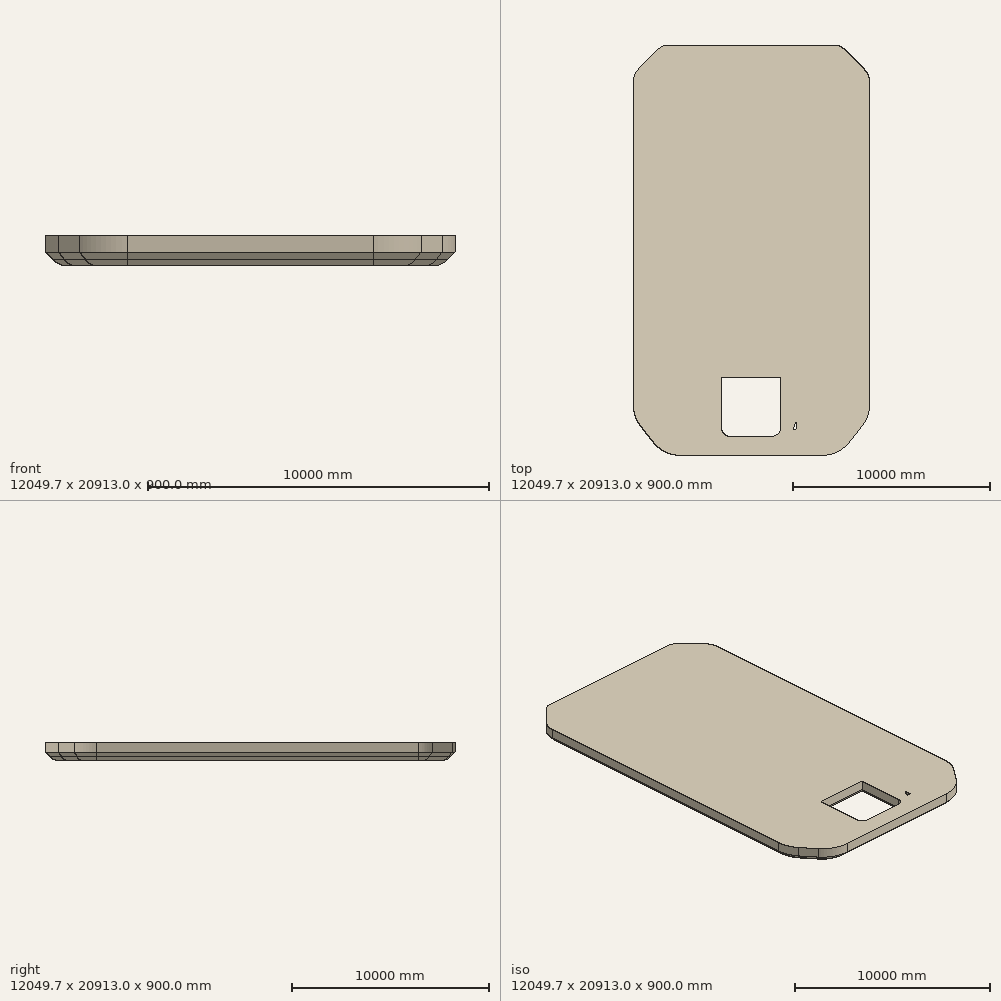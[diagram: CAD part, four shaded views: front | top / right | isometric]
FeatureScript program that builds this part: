
annotation { "Feature Type Name" : "Feature", "Feature Type Description" : "" }
export const myFeature = defineFeature(function(context is Context, id is Id, definition is map)
    precondition{}
    {
        {
            var Q0;
            Q0=qCreatedBy(makeId("Top.planeOp"),FACE);
            var sketch = newSketch(context, id + "F0", { "sketchPlane" : qUnion([Q0])});
            skLineSegment(sketch, "E0.bottom", {"start": v(-3604.76, -10456.52) * mm, "end": v(3572.95, -10456.52) * mm});
            skLineSegment(sketch, "E0.top", {"start": v(-4294.95, 10456.52) * mm, "end": v(4334.31, 10456.52) * mm});
            skLineSegment(sketch, "E0.left", {"start": v(-6024.84, -7867.65) * mm, "end": v(-6024.84, 8560.94) * mm});
            skPoint(sketch, "E0.middle", {"position": v(0, 0) * mm});
            skPoint(sketch, "E1.visualSharp", {"position": v(-6024.84, -10456.52) * mm});
            skLineSegment(sketch, "E2", {"start": v(0, 0) * mm, "end": v(0, -15471.61) * mm, "construction": true});
            skLineSegment(sketch, "E3.0", {"start": v(-4500, 12642.06) * mm, "end": v(-4500, -15471.61) * mm, "construction": true});
            skLineSegment(sketch, "E4.MirrorCS", {"start": v(4500, 12642.06) * mm, "end": v(4500, -15471.61) * mm, "construction": true});
            skLineSegment(sketch, "E5", {"start": v(-5019.92, -9768.88) * mm, "end": v(-5640, -8980) * mm});
            skPoint(sketch, "E6.newPointA", {"position": v(-5200, -10456.52) * mm});
            skPoint(sketch, "E6.newPointB", {"position": v(-4479.4, -10456.52) * mm});
            skArc(sketch, "E6.filletArc", {"start": v(-5019.92, -9768.88) * mm, "mid": v(-4391.45, -10275.51) * mm, "end": v(-3604.76, -10456.52) * mm});
            skArc(sketch, "E7.filletArc", {"start": v(-6024.84, -7867.65) * mm, "mid": v(-5925.91, -8456.17) * mm, "end": v(-5640, -8980) * mm});
            skPoint(sketch, "E8.newPointA", {"position": v(5975.16, -10456.52) * mm});
            skLineSegment(sketch, "E9", {"start": v(6000, 10500) * mm, "end": v(10945.39, 10500) * mm, "construction": true});
            skLineSegment(sketch, "E10.0", {"start": v(6000, 9000) * mm, "end": v(10945.39, 9000) * mm, "construction": true});
            skLineSegment(sketch, "E11.MirrorCS", {"start": v(0, 18000) * mm, "end": v(0, 33471.61) * mm, "construction": true});
            skLineSegment(sketch, "E12.MirrorCS", {"start": v(-4719.21, 10280.79) * mm, "end": v(-5731.95, 9268.05) * mm});
            skPoint(sketch, "E13.newPointA", {"position": v(-6000, 9000) * mm});
            skPoint(sketch, "E13.newPointB", {"position": v(-6024.84, 10543.48) * mm});
            skArc(sketch, "E13.filletArc", {"start": v(-5731.95, 9268.05) * mm, "mid": v(-5948.72, 8943.63) * mm, "end": v(-6024.84, 8560.94) * mm});
            skPoint(sketch, "E14.newPointA", {"position": v(-4500, 10500) * mm});
            skPoint(sketch, "E14.newPointB", {"position": v(-5975.16, 10456.52) * mm});
            skArc(sketch, "E14.filletArc", {"start": v(-4294.95, 10456.52) * mm, "mid": v(-4524.56, 10410.85) * mm, "end": v(-4719.21, 10280.79) * mm});
            skPoint(sketch, "E15.newPointA", {"position": v(6000, 9000) * mm});
            skPoint(sketch, "E16.newPointA", {"position": v(4500, 10500) * mm});
            skPoint(sketch, "E16.newPointB", {"position": v(6024.84, 10456.52) * mm});
            skLineSegment(sketch, "E17.MirrorCS", {"start": v(3604.76, -10456.52) * mm, "end": v(-3572.95, -10456.52) * mm});
            skArc(sketch, "E18.MirrorCS", {"start": v(5019.92, -9768.88) * mm, "mid": v(4391.45, -10275.51) * mm, "end": v(3604.76, -10456.52) * mm});
            skLineSegment(sketch, "E19.MirrorCS", {"start": v(5019.92, -9768.88) * mm, "end": v(5640, -8980) * mm});
            skArc(sketch, "E20.MirrorCS", {"start": v(6024.84, -7867.65) * mm, "mid": v(5925.91, -8456.17) * mm, "end": v(5640, -8980) * mm});
            skLineSegment(sketch, "E21.MirrorCS", {"start": v(6024.84, -7867.65) * mm, "end": v(6024.84, 8560.94) * mm});
            skArc(sketch, "E22.MirrorCS", {"start": v(5731.95, 9268.05) * mm, "mid": v(5948.72, 8943.63) * mm, "end": v(6024.84, 8560.94) * mm});
            skLineSegment(sketch, "E23.MirrorCS", {"start": v(4719.21, 10280.79) * mm, "end": v(5731.95, 9268.05) * mm});
            skArc(sketch, "E24.MirrorCS", {"start": v(4294.95, 10456.52) * mm, "mid": v(4524.56, 10410.85) * mm, "end": v(4719.21, 10280.79) * mm});
            skPoint(sketch, "E25", {"position": v(-1520, -6476.52) * mm});
            skPoint(sketch, "E26", {"position": v(-1520, -9476.52) * mm});
            skPoint(sketch, "E27", {"position": v(1480, -9476.52) * mm});
            skPoint(sketch, "E28", {"position": v(1480, -6476.52) * mm});
            skLineSegment(sketch, "E29", {"start": v(-1520, -6476.52) * mm, "end": v(1480, -6476.52) * mm});
            skLineSegment(sketch, "E30", {"start": v(1080, -9476.52) * mm, "end": v(-1120, -9476.52) * mm});
            skLineSegment(sketch, "E31", {"start": v(-1520, -6476.52) * mm, "end": v(-1520, -9076.52) * mm});
            skLineSegment(sketch, "E32", {"start": v(1480, -6476.52) * mm, "end": v(1480, -9076.52) * mm});
            skArc(sketch, "E33.filletArc", {"start": v(-1520, -9076.52) * mm, "mid": v(-1402.84, -9359.37) * mm, "end": v(-1120, -9476.52) * mm});
            skArc(sketch, "E34.filletArc", {"start": v(1080, -9476.52) * mm, "mid": v(1362.84, -9359.37) * mm, "end": v(1480, -9076.52) * mm});
            skPoint(sketch, "E35", {"position": v(-20, -6476.52) * mm});
            skPoint(sketch, "E36", {"position": v(-20, -9476.52) * mm});
            skLineSegment(sketch, "E37.0", {"start": v(-650, 0) * mm, "end": v(-650, -15471.61) * mm, "construction": true});
            skPoint(sketch, "E38", {"position": v(-650, -9156.52) * mm});
            skPoint(sketch, "E39", {"position": v(-650, -8906.52) * mm});
            skLineSegment(sketch, "E40", {"start": v(-650, -8906.52) * mm, "end": v(-1228.06, -8668.5) * mm});
            skLineSegment(sketch, "E41", {"start": v(2294.01, -8720.57) * mm, "end": v(2514.01, -8720.57) * mm, "construction": true});
            skLineSegment(sketch, "E42", {"start": v(2294.01, -8720.57) * mm, "end": v(2109.42, -9152.8) * mm});
            skLineSegment(sketch, "E43", {"start": v(2109.42, -9152.8) * mm, "end": v(2294.01, -9152.8) * mm});
            skLineSegment(sketch, "E44", {"start": v(2294.01, -8720.57) * mm, "end": v(2294.01, -9445.98) * mm});
            skLineSegment(sketch, "E45.0", {"start": v(1100, -8721.92) * mm, "end": v(1098.33, -8721.92) * mm});
            skLineSegment(sketch, "E46.0", {"start": v(-613.48, -8721.92) * mm, "end": v(-1043.46, -8544.88) * mm});
            skLineSegment(sketch, "E47.0", {"start": v(-699.45, -9156.52) * mm, "end": v(-1478.06, -8835.94) * mm});
            skLineSegment(sketch, "E48", {"start": v(-1043.46, -8544.88) * mm, "end": v(-1043.46, -8044.88) * mm});
            skLineSegment(sketch, "E49.0", {"start": v(-1228.06, -8668.5) * mm, "end": v(-1228.06, -8044.88) * mm});
            skLineSegment(sketch, "E50.0", {"start": v(-1478.06, -8835.94) * mm, "end": v(-1478.06, -8044.88) * mm});
            skLineSegment(sketch, "E51", {"start": v(-1478.06, -8044.88) * mm, "end": v(-1043.46, -8044.88) * mm});
            skLineSegment(sketch, "E52.MirrorCS", {"start": v(699.45, -9156.52) * mm, "end": v(1478.06, -8835.94) * mm});
            skLineSegment(sketch, "E53.MirrorCS", {"start": v(650, -8906.52) * mm, "end": v(1228.06, -8668.5) * mm});
            skLineSegment(sketch, "E54.MirrorCS", {"start": v(613.48, -8721.92) * mm, "end": v(1043.46, -8544.88) * mm});
            skLineSegment(sketch, "E55.MirrorCS", {"start": v(1043.46, -8544.88) * mm, "end": v(1043.46, -8044.88) * mm});
            skLineSegment(sketch, "E56.MirrorCS", {"start": v(1228.06, -8668.5) * mm, "end": v(1228.06, -8044.88) * mm});
            skLineSegment(sketch, "E57.MirrorCS", {"start": v(1478.06, -8835.94) * mm, "end": v(1478.06, -8044.88) * mm});
            skLineSegment(sketch, "E58.MirrorCS", {"start": v(1478.06, -8044.88) * mm, "end": v(1043.46, -8044.88) * mm});
            skLineSegment(sketch, "E59", {"start": v(613.48, -8721.92) * mm, "end": v(699.45, -9156.52) * mm});
            skLineSegment(sketch, "E60", {"start": v(-613.48, -8721.92) * mm, "end": v(-699.45, -9156.52) * mm});
            skLineSegment(sketch, "E61", {"start": v(1043.46, -8544.88) * mm, "end": v(1228.06, -8668.5) * mm});
            skLineSegment(sketch, "E62.0", {"start": v(252, -7876.52) * mm, "end": v(-252, -7876.52) * mm});
            skLineSegment(sketch, "E63.0", {"start": v(1080, -8416.52) * mm, "end": v(1043.46, -8416.52) * mm});
            skLineSegment(sketch, "E64.0", {"start": v(-252, 0) * mm, "end": v(-252, -6476.52) * mm, "construction": true});
            skLineSegment(sketch, "E65.MirrorCS", {"start": v(252, 0) * mm, "end": v(252, -6476.52) * mm, "construction": true});
            skPoint(sketch, "E66", {"position": v(-252, -7876.52) * mm});
            skPoint(sketch, "E67", {"position": v(-252, -8416.52) * mm});
            skPoint(sketch, "E68", {"position": v(252, -8416.52) * mm});
            skPoint(sketch, "E69", {"position": v(252, -7876.52) * mm});
            skLineSegment(sketch, "E70.0", {"start": v(232, -7796.52) * mm, "end": v(-232, -7796.52) * mm});
            skLineSegment(sketch, "E71.0", {"start": v(252, -7961.52) * mm, "end": v(-252, -7961.52) * mm});
            skPoint(sketch, "E72", {"position": v(-252, -7796.52) * mm});
            skPoint(sketch, "E73", {"position": v(252, -7796.52) * mm});
            skPoint(sketch, "E74", {"position": v(-252, -7961.52) * mm});
            skPoint(sketch, "E75", {"position": v(252, -7961.52) * mm});
            skPoint(sketch, "E76", {"position": v(-20, -7961.52) * mm});
            skPoint(sketch, "E77", {"position": v(-20, -8416.52) * mm});
            skPoint(sketch, "E78.orphan", {"position": v(-1120, -7961.52) * mm});
            skPoint(sketch, "E79.orphan", {"position": v(1080, -7961.52) * mm});
            skLineSegment(sketch, "E80.trimOffspring", {"start": v(232, -8416.52) * mm, "end": v(-232, -8416.52) * mm});
            skLineSegment(sketch, "E81.trimOffspring", {"start": v(-650, -8416.52) * mm, "end": v(-1120, -8416.52) * mm});
            skLineSegment(sketch, "E82.trimOffspring", {"start": v(252, -7816.52) * mm, "end": v(252, -8396.52) * mm});
            skLineSegment(sketch, "E83.trimOffspring", {"start": v(252, -9476.52) * mm, "end": v(252, -15471.61) * mm, "construction": true});
            skLineSegment(sketch, "E84.trimOffspring", {"start": v(-252, -9476.52) * mm, "end": v(-252, -15471.61) * mm, "construction": true});
            skLineSegment(sketch, "E85.trimOffspring", {"start": v(-252, -7816.52) * mm, "end": v(-252, -8396.52) * mm});
            skArc(sketch, "E86.filletArc", {"start": v(-232, -7796.52) * mm, "mid": v(-246.14, -7802.38) * mm, "end": v(-252, -7816.52) * mm});
            skArc(sketch, "E87.filletArc", {"start": v(252, -7816.52) * mm, "mid": v(246.14, -7802.38) * mm, "end": v(232, -7796.52) * mm});
            skArc(sketch, "E88.filletArc", {"start": v(-252, -8396.52) * mm, "mid": v(-246.14, -8410.67) * mm, "end": v(-232, -8416.52) * mm});
            skArc(sketch, "E89.filletArc", {"start": v(232, -8416.52) * mm, "mid": v(246.14, -8410.67) * mm, "end": v(252, -8396.52) * mm});
            skLineSegment(sketch, "E90", {"start": v(-252, -7876.52) * mm, "end": v(-211.63, -7961.52) * mm});
            skLineSegment(sketch, "E91", {"start": v(-211.63, -7961.52) * mm, "end": v(-252, -8396.52) * mm});
            skLineSegment(sketch, "E92.MirrorCS", {"start": v(211.63, -7961.52) * mm, "end": v(252, -8396.52) * mm});
            skLineSegment(sketch, "E93.MirrorCS", {"start": v(252, -7876.52) * mm, "end": v(211.63, -7961.52) * mm});
            skLineSegment(sketch, "E94", {"start": v(-275.38, -8401.43) * mm, "end": v(-495.38, -8401.43) * mm});
            skLineSegment(sketch, "E95", {"start": v(-275.38, -8401.43) * mm, "end": v(-275.38, -8040.14) * mm});
            skLineSegment(sketch, "E96", {"start": v(-275.38, -8040.14) * mm, "end": v(-252, -7961.52) * mm});
            skLineSegment(sketch, "E97", {"start": v(-495.38, -8401.43) * mm, "end": v(-495.38, -8316.43) * mm});
            skLineSegment(sketch, "E98", {"start": v(-495.38, -8316.43) * mm, "end": v(-410.38, -8316.43) * mm});
            skLineSegment(sketch, "E99", {"start": v(-410.38, -8316.43) * mm, "end": v(-410.38, -8235.04) * mm});
            skLineSegment(sketch, "E100", {"start": v(-410.38, -8235.04) * mm, "end": v(-356.33, -8040.14) * mm});
            skLineSegment(sketch, "E101", {"start": v(-356.33, -8040.14) * mm, "end": v(-252, -7876.52) * mm});
            skSolve(sketch);
        }
        {
            var Q0;
            Q0=makeQuery(id+"F0.imprint","IMPRINT",FACE,{"disambiguationData":[TD([[makeQuery(id+"F0.imprint","IMPRINT",EDGE,{"derivedFrom":sQuery(id+"F0.wireOp",EDGE,"E0.bottom")}),1.0]])]});
            extrude(context, id + "F1", {"entities" : qUnion([Q0]), "depth" : 500 * mm});
        }
        {
            var Q0;
            Q0=makeQuery(id+"F1.opExtrude","CAP_FACE",FACE,{"disambiguationData":[OSD([sQuery(id+"F0.wireOp",EDGE,"E0.bottom"),sQuery(id+"F0.wireOp",EDGE,"E0.top"),sQuery(id+"F0.wireOp",EDGE,"E0.left"),sQuery(id+"F0.wireOp",EDGE,"E0.right")])],"isStart":true});
            extrude(context, id + "F2", {"entities" : qUnion([Q0]), "operationType" : NewBodyOperationType.ADD, "depth" : 400 * mm, "hasDraft" : true, "draftAngle" : 45 * degree, "draftPullDirection" : true});
        }
        {
            var Q0;
            Q0=makeQuery(id+"F2.opExtrude","CAP_EDGE",EDGE,{"disambiguationData":[OSD([sQuery(id+"F0.wireOp",EDGE,"E0.bottom")])],"isStart":false});
            var Q1;
            Q1=makeQuery(id+"F2.opExtrude","CAP_EDGE",EDGE,{"disambiguationData":[OSD([sQuery(id+"F0.wireOp",EDGE,"E0.right")])],"isStart":false});
            fillet(context, id + "F3", {"entities" : qUnion([Q0, Q1]), "radius" : 600 * mm, "tangentPropagation" : true, "allowEdgeOverflow" : false});
        }
    });
